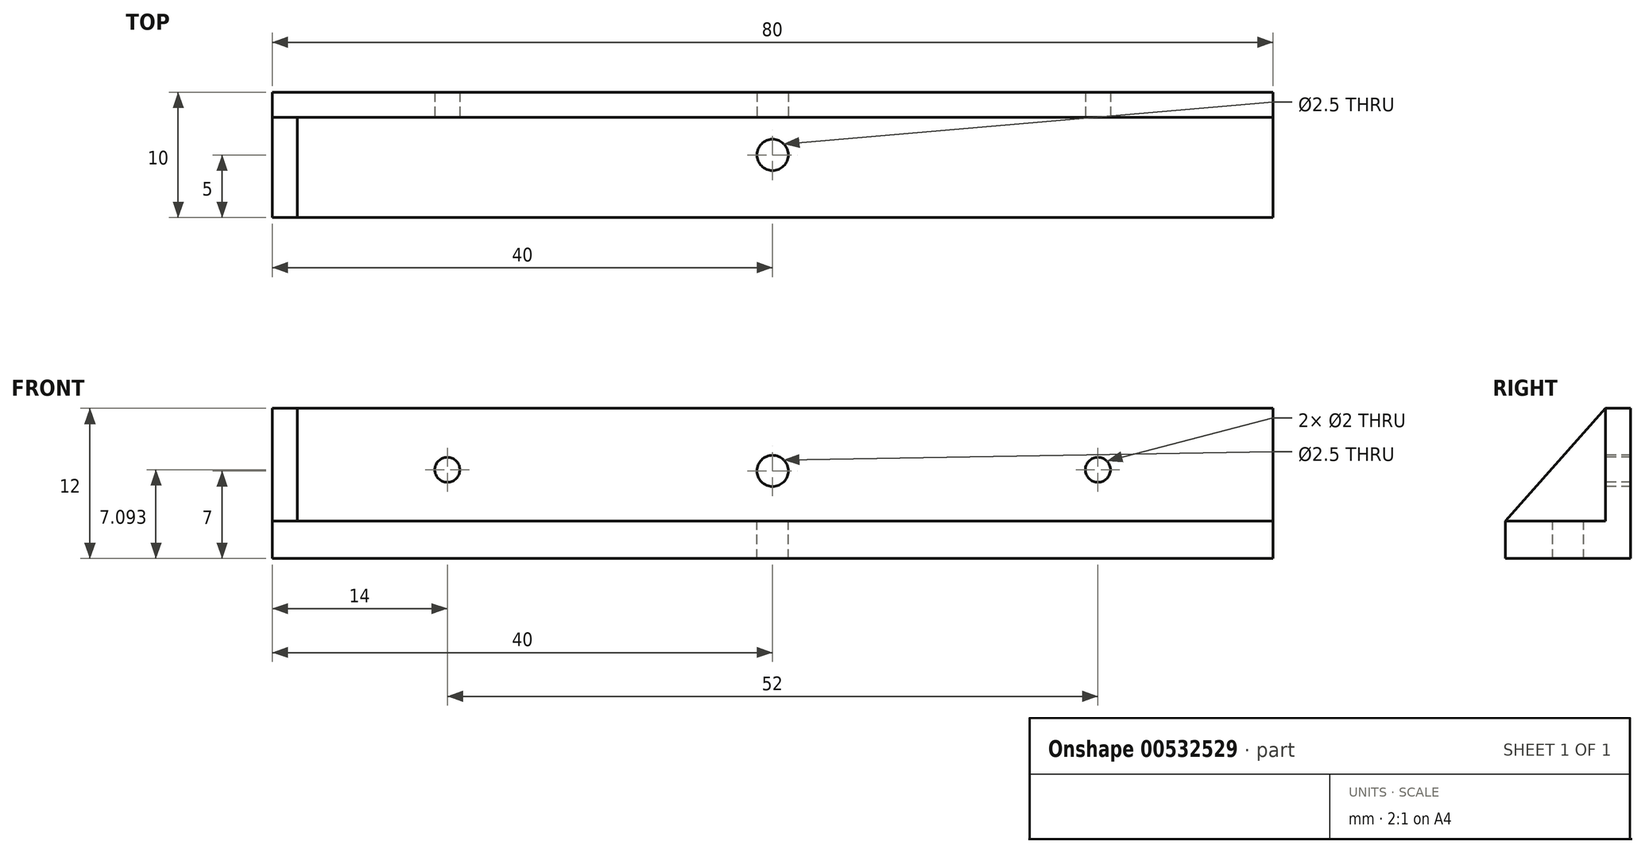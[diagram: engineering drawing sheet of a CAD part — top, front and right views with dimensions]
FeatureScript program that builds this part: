
annotation { "Feature Type Name" : "Feature", "Feature Type Description" : "" }
export const myFeature = defineFeature(function(context is Context, id is Id, definition is map)
    precondition{}
    {
        {
            var Q0;
            Q0=qCreatedBy(makeId("Top.planeOp"),FACE);
            var sketch = newSketch(context, id + "F0", { "sketchPlane" : qUnion([Q0])});
            skLineSegment(sketch, "E0.bottom", {"start": v(40, -5) * mm, "end": v(-40, -5) * mm});
            skLineSegment(sketch, "E0.top", {"start": v(40, 5) * mm, "end": v(-40, 5) * mm});
            skLineSegment(sketch, "E0.left", {"start": v(40, -5) * mm, "end": v(40, 5) * mm});
            skLineSegment(sketch, "E0.right", {"start": v(-40, -5) * mm, "end": v(-40, 5) * mm});
            skPoint(sketch, "E0.middle", {"position": v(0, 0) * mm});
            skSolve(sketch);
        }
        {
            var Q0;
            Q0=makeQuery(id+"F0.imprint","IMPRINT",FACE,{"disambiguationData":[TD([[makeQuery(id+"F0.imprint","IMPRINT",EDGE,{"derivedFrom":sQuery(id+"F0.wireOp",EDGE,"E0.bottom")}),-1.0]])]});
            extrude(context, id + "F1", {"entities" : qUnion([Q0]), "depth" : 3 * mm, "offsetDistance" : 25 * mm});
        }
        {
            var Q0;
            Q0=makeQuery(id+"F1.opExtrude","CAP_FACE",FACE,{"disambiguationData":[OSD([sQuery(id+"F0.wireOp",EDGE,"E0.bottom"),sQuery(id+"F0.wireOp",EDGE,"E0.top"),sQuery(id+"F0.wireOp",EDGE,"E0.left"),sQuery(id+"F0.wireOp",EDGE,"E0.right")])],"isStart":false});
            var sketch = newSketch(context, id + "F2", { "sketchPlane" : qUnion([Q0])});
            skLineSegment(sketch, "E1.bottom", {"start": v(-40, 5) * mm, "end": v(40, 5) * mm});
            skLineSegment(sketch, "E1.top", {"start": v(-40, 3) * mm, "end": v(40, 3) * mm});
            skLineSegment(sketch, "E1.left", {"start": v(-40, 5) * mm, "end": v(-40, 3) * mm});
            skLineSegment(sketch, "E1.right", {"start": v(40, 5) * mm, "end": v(40, 3) * mm});
            skSolve(sketch);
        }
        {
            var Q0;
            Q0=makeQuery(id+"F2.imprint","IMPRINT",FACE,{"disambiguationData":[TD([[makeQuery(id+"F2.imprint","IMPRINT",EDGE,{"derivedFrom":sQuery(id+"F2.wireOp",EDGE,"E1.bottom")}),1.0]])]});
            extrude(context, id + "F3", {"entities" : qUnion([Q0]), "operationType" : NewBodyOperationType.ADD, "depth" : 9 * mm, "offsetDistance" : 25 * mm});
        }
        {
            var Q0;
            Q0=makeQuery(id+"F1.opExtrude","CAP_FACE",FACE,{"disambiguationData":[OSD([sQuery(id+"F0.wireOp",EDGE,"E0.bottom"),sQuery(id+"F0.wireOp",EDGE,"E0.top"),sQuery(id+"F0.wireOp",EDGE,"E0.left"),sQuery(id+"F0.wireOp",EDGE,"E0.right")])],"isStart":false});
            var sketch = newSketch(context, id + "F4", { "sketchPlane" : qUnion([Q0])});
            skCircle(sketch, "E2", {"center": v(0, 0) * mm, "radius": 1.25 * mm});
            skSolve(sketch);
        }
        {
            var Q0;
            Q0=makeQuery(id+"F4.imprint","IMPRINT",FACE,{"disambiguationData":[TD([[makeQuery(id+"F4.imprint","IMPRINT",EDGE,{"derivedFrom":sQuery(id+"F4.wireOp",EDGE,"E2")}),1.0]])]});
            extrude(context, id + "F5", {"entities" : qUnion([Q0]), "operationType" : NewBodyOperationType.REMOVE, "endBound" : BoundingType.THROUGH_ALL, "oppositeDirection" : true, "depth" : 25 * mm, "offsetDistance" : 25 * mm});
        }
        {
            var Q0;
            Q0=makeQuery(id+"F3.opExtrude","SWEPT_FACE",FACE,{"disambiguationData":[OSD([sQuery(id+"F2.wireOp",EDGE,"E1.top")])]});
            var sketch = newSketch(context, id + "F6", { "sketchPlane" : qUnion([Q0])});
            skCircle(sketch, "E3", {"center": v(0, 7) * mm, "radius": 1.25 * mm});
            skSolve(sketch);
        }
        {
            var Q0;
            Q0=makeQuery(id+"F6.imprint","IMPRINT",FACE,{"disambiguationData":[TD([[makeQuery(id+"F6.imprint","IMPRINT",EDGE,{"derivedFrom":sQuery(id+"F6.wireOp",EDGE,"E3")}),1.0]])]});
            extrude(context, id + "F7", {"entities" : qUnion([Q0]), "operationType" : NewBodyOperationType.REMOVE, "endBound" : BoundingType.THROUGH_ALL, "oppositeDirection" : true, "depth" : 25 * mm, "offsetDistance" : 25 * mm});
        }
        {
            var Q0;
            Q0=makeQuery(id+"F3.boolean.opBoolean","MERGE",FACE,{"derivedFrom":[makeQuery(id+"F1.opExtrude","SWEPT_FACE",FACE,{"disambiguationData":[OSD([sQuery(id+"F0.wireOp",EDGE,"E0.right")])]}),makeQuery(id+"F3.opExtrude","SWEPT_FACE",FACE,{"disambiguationData":[OSD([sQuery(id+"F2.wireOp",EDGE,"E1.left")])]})]});
            var sketch = newSketch(context, id + "F8", { "sketchPlane" : qUnion([Q0])});
            skLineSegment(sketch, "E4", {"start": v(-3, 12) * mm, "end": v(5, 3) * mm});
            skLineSegment(sketch, "E5", {"start": v(5, 3) * mm, "end": v(-3, 3) * mm});
            skLineSegment(sketch, "E6", {"start": v(-3, 3) * mm, "end": v(-3, 12) * mm});
            skSolve(sketch);
        }
        {
            var Q0;
            Q0=makeQuery(id+"F8.imprint","IMPRINT",FACE,{"disambiguationData":[TD([[makeQuery(id+"F8.imprint","IMPRINT",EDGE,{"derivedFrom":sQuery(id+"F8.wireOp",EDGE,"E4")}),-1.0]])]});
            extrude(context, id + "F9", {"entities" : qUnion([Q0]), "operationType" : NewBodyOperationType.ADD, "oppositeDirection" : true, "depth" : 2 * mm, "offsetDistance" : 25 * mm});
        }
        {
            var Q0;
            Q0=makeQuery(id+"F3.opExtrude","SWEPT_FACE",FACE,{"disambiguationData":[OSD([sQuery(id+"F2.wireOp",EDGE,"E1.top")])]});
            var sketch = newSketch(context, id + "F10", { "sketchPlane" : qUnion([Q0])});
            skCircle(sketch, "E7", {"center": v(26, 7.1) * mm, "radius": 1 * mm});
            skCircle(sketch, "E8", {"center": v(-26, 7.1) * mm, "radius": 1 * mm});
            skSolve(sketch);
        }
        {
            var Q0;
            Q0=makeQuery(id+"F10.imprint","IMPRINT",FACE,{"disambiguationData":[TD([[makeQuery(id+"F10.imprint","IMPRINT",EDGE,{"derivedFrom":sQuery(id+"F10.wireOp",EDGE,"E8")}),1.0]])]});
            var Q1;
            Q1=makeQuery(id+"F10.imprint","IMPRINT",FACE,{"disambiguationData":[TD([[makeQuery(id+"F10.imprint","IMPRINT",EDGE,{"derivedFrom":sQuery(id+"F10.wireOp",EDGE,"E7")}),1.0]])]});
            extrude(context, id + "F11", {"entities" : qUnion([Q0, Q1]), "operationType" : NewBodyOperationType.REMOVE, "endBound" : BoundingType.THROUGH_ALL, "oppositeDirection" : true, "depth" : 25 * mm, "offsetDistance" : 25 * mm});
        }
    });
